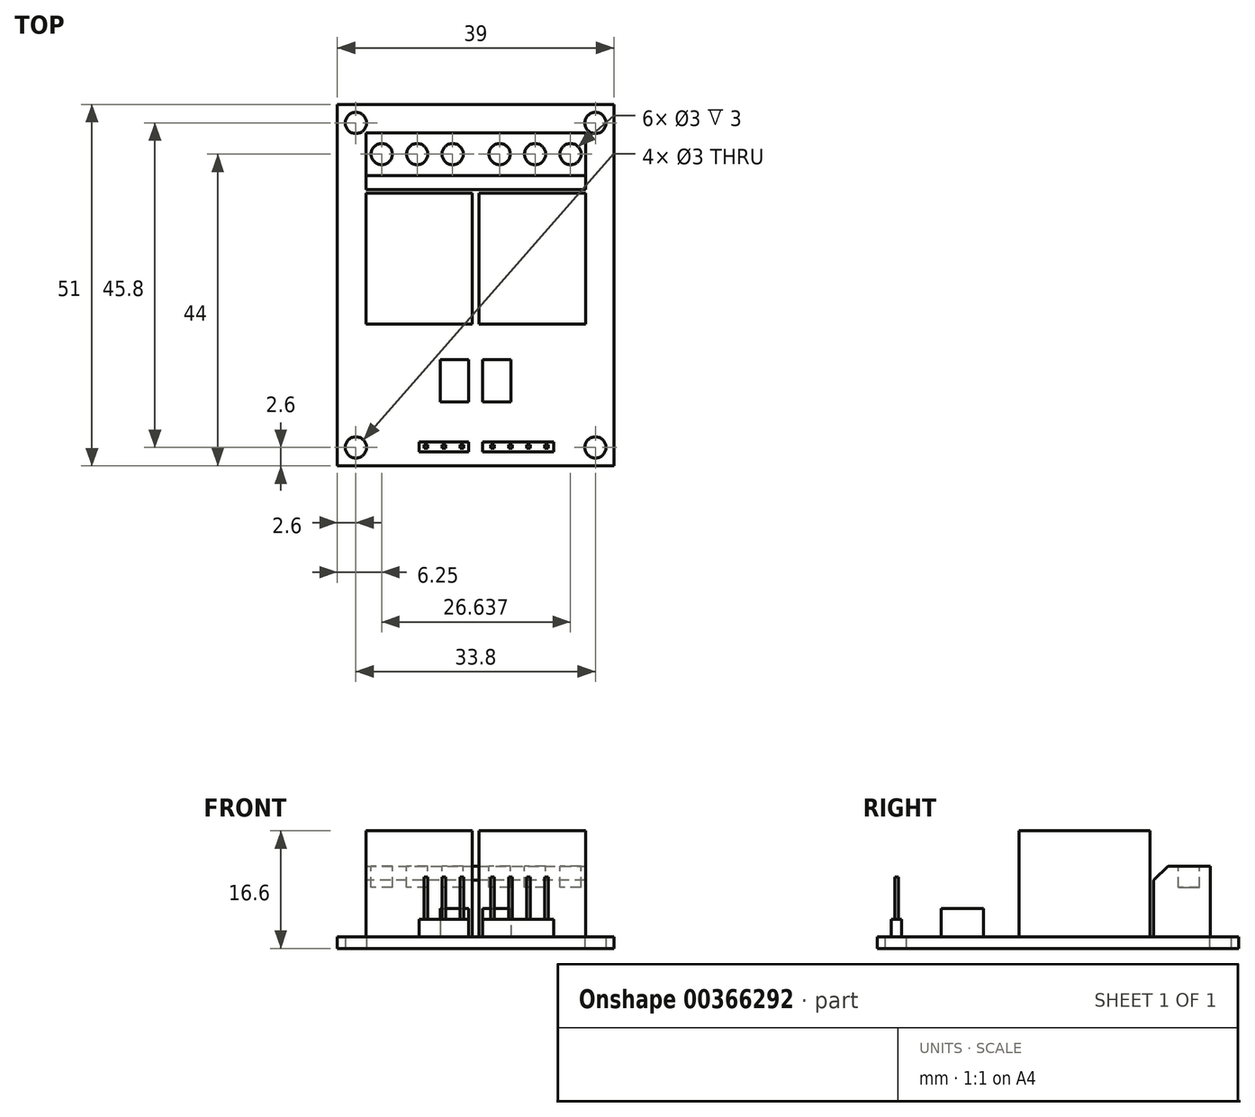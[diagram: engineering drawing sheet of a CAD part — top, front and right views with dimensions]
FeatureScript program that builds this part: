
annotation { "Feature Type Name" : "Feature", "Feature Type Description" : "" }
export const myFeature = defineFeature(function(context is Context, id is Id, definition is map)
    precondition{}
    {
        {
            var Q0;
            Q0=qCreatedBy(makeId("Top.planeOp"),FACE);
            var sketch = newSketch(context, id + "F0", { "sketchPlane" : qUnion([Q0])});
            skLineSegment(sketch, "E0.bottom", {"start": v(19.5, -25.5) * mm, "end": v(-19.5, -25.5) * mm});
            skLineSegment(sketch, "E0.top", {"start": v(19.5, 25.5) * mm, "end": v(-19.5, 25.5) * mm});
            skLineSegment(sketch, "E0.left", {"start": v(19.5, -25.5) * mm, "end": v(19.5, 25.5) * mm});
            skLineSegment(sketch, "E0.right", {"start": v(-19.5, -25.5) * mm, "end": v(-19.5, 25.5) * mm});
            skPoint(sketch, "E0.middle", {"position": v(0, 0) * mm});
            skPoint(sketch, "E1", {"position": v(-16.9, 22.9) * mm});
            skPoint(sketch, "E2", {"position": v(16.9, 22.9) * mm});
            skPoint(sketch, "E3", {"position": v(16.9, -22.9) * mm});
            skPoint(sketch, "E4", {"position": v(-16.9, -22.9) * mm});
            skCircle(sketch, "E5", {"center": v(-16.9, 22.9) * mm, "radius": 1.5 * mm});
            skCircle(sketch, "E6", {"center": v(16.9, 22.9) * mm, "radius": 1.5 * mm});
            skCircle(sketch, "E7", {"center": v(16.9, -22.9) * mm, "radius": 1.5 * mm});
            skCircle(sketch, "E8", {"center": v(-16.9, -22.9) * mm, "radius": 1.5 * mm});
            skSolve(sketch);
        }
        {
            var Q0;
            Q0=makeQuery(id+"F0.imprint","IMPRINT",FACE,{"disambiguationData":[TD([[makeQuery(id+"F0.imprint","IMPRINT",EDGE,{"derivedFrom":sQuery(id+"F0.wireOp",EDGE,"E0.bottom")}),-1.0]])]});
            extrude(context, id + "F1", {"entities" : qUnion([Q0]), "depth" : 1.6 * mm});
        }
        {
            var Q0;
            Q0=makeQuery(id+"F1.opExtrude","CAP_FACE",FACE,{"disambiguationData":[OSD([sQuery(id+"F0.wireOp",EDGE,"E0.bottom"),sQuery(id+"F0.wireOp",EDGE,"E0.top"),sQuery(id+"F0.wireOp",EDGE,"E0.left"),sQuery(id+"F0.wireOp",EDGE,"E0.right"),sQuery(id+"F0.wireOp",EDGE,"E5"),sQuery(id+"F0.wireOp",EDGE,"E6"),sQuery(id+"F0.wireOp",EDGE,"E7"),sQuery(id+"F0.wireOp",EDGE,"E8")])],"isStart":false});
            var sketch = newSketch(context, id + "F2", { "sketchPlane" : qUnion([Q0])});
            skLineSegment(sketch, "E9.bottom", {"start": v(-15.5, 13) * mm, "end": v(-0.5, 13) * mm});
            skLineSegment(sketch, "E9.top", {"start": v(-15.5, -5.5) * mm, "end": v(-0.5, -5.5) * mm});
            skLineSegment(sketch, "E9.left", {"start": v(-15.5, 13) * mm, "end": v(-15.5, -5.5) * mm});
            skLineSegment(sketch, "E9.right", {"start": v(-0.5, 13) * mm, "end": v(-0.5, -5.5) * mm});
            skLineSegment(sketch, "E10.bottom", {"start": v(0.5, 13) * mm, "end": v(15.5, 13) * mm});
            skLineSegment(sketch, "E10.top", {"start": v(0.5, -5.5) * mm, "end": v(15.5, -5.5) * mm});
            skLineSegment(sketch, "E10.left", {"start": v(0.5, 13) * mm, "end": v(0.5, -5.5) * mm});
            skLineSegment(sketch, "E10.right", {"start": v(15.5, 13) * mm, "end": v(15.5, -5.5) * mm});
            skSolve(sketch);
        }
        {
            var Q0;
            Q0=makeQuery(id+"F2.imprint","IMPRINT",FACE,{"disambiguationData":[TD([[makeQuery(id+"F2.imprint","IMPRINT",EDGE,{"derivedFrom":sQuery(id+"F2.wireOp",EDGE,"E9.bottom")}),-1.0]])]});
            var Q1;
            Q1=makeQuery(id+"F2.imprint","IMPRINT",FACE,{"disambiguationData":[TD([[makeQuery(id+"F2.imprint","IMPRINT",EDGE,{"derivedFrom":sQuery(id+"F2.wireOp",EDGE,"E10.bottom")}),-1.0]])]});
            extrude(context, id + "F3", {"entities" : qUnion([Q0, Q1]), "operationType" : NewBodyOperationType.ADD, "depth" : 15 * mm});
        }
        {
            var Q0;
            Q0=makeQuery(id+"F1.opExtrude","CAP_FACE",FACE,{"disambiguationData":[OSD([sQuery(id+"F0.wireOp",EDGE,"E0.bottom"),sQuery(id+"F0.wireOp",EDGE,"E0.top"),sQuery(id+"F0.wireOp",EDGE,"E0.left"),sQuery(id+"F0.wireOp",EDGE,"E0.right"),sQuery(id+"F0.wireOp",EDGE,"E5"),sQuery(id+"F0.wireOp",EDGE,"E6"),sQuery(id+"F0.wireOp",EDGE,"E7"),sQuery(id+"F0.wireOp",EDGE,"E8")])],"isStart":false});
            var sketch = newSketch(context, id + "F4", { "sketchPlane" : qUnion([Q0])});
            skLineSegment(sketch, "E11.bottom", {"start": v(-15.5, 21.5) * mm, "end": v(15.5, 21.5) * mm});
            skLineSegment(sketch, "E11.top", {"start": v(-15.5, 13.5) * mm, "end": v(15.5, 13.5) * mm});
            skLineSegment(sketch, "E11.left", {"start": v(-15.5, 21.5) * mm, "end": v(-15.5, 13.5) * mm});
            skLineSegment(sketch, "E11.right", {"start": v(15.5, 21.5) * mm, "end": v(15.5, 13.5) * mm});
            skSolve(sketch);
        }
        {
            var Q0;
            Q0=makeQuery(id+"F4.imprint","IMPRINT",FACE,{"disambiguationData":[TD([[makeQuery(id+"F4.imprint","IMPRINT",EDGE,{"derivedFrom":sQuery(id+"F4.wireOp",EDGE,"E11.bottom")}),-1.0]])]});
            extrude(context, id + "F5", {"entities" : qUnion([Q0]), "operationType" : NewBodyOperationType.ADD, "depth" : 10 * mm});
        }
        {
            var Q0;
            Q0=makeQuery(id+"F5.opExtrude","CAP_EDGE",EDGE,{"disambiguationData":[OSD([sQuery(id+"F4.wireOp",EDGE,"E11.top")])],"isStart":false});
            chamfer(context, id + "F6", {"entities" : qUnion([Q0]), "width" : 2 * mm, "tangentPropagation" : true});
        }
        {
            var Q0;
            Q0=makeQuery(id+"F5.opExtrude","CAP_FACE",FACE,{"disambiguationData":[OSD([sQuery(id+"F4.wireOp",EDGE,"E11.bottom"),sQuery(id+"F4.wireOp",EDGE,"E11.top"),sQuery(id+"F4.wireOp",EDGE,"E11.left"),sQuery(id+"F4.wireOp",EDGE,"E11.right")])],"isStart":false});
            var sketch = newSketch(context, id + "F7", { "sketchPlane" : qUnion([Q0])});
            skCircle(sketch, "E12", {"center": v(-13.25, 18.5) * mm, "radius": 1.5 * mm});
            skCircle(sketch, "E13", {"center": v(-8.25, 18.5) * mm, "radius": 1.5 * mm});
            skCircle(sketch, "E14", {"center": v(-3.25, 18.5) * mm, "radius": 1.5 * mm});
            skCircle(sketch, "E15", {"center": v(3.39, 18.5) * mm, "radius": 1.5 * mm});
            skCircle(sketch, "E16", {"center": v(8.39, 18.5) * mm, "radius": 1.5 * mm});
            skCircle(sketch, "E17", {"center": v(13.39, 18.5) * mm, "radius": 1.5 * mm});
            skSolve(sketch);
        }
        {
            var Q0;
            Q0=makeQuery(id+"F7.imprint","IMPRINT",FACE,{"disambiguationData":[TD([[makeQuery(id+"F7.imprint","IMPRINT",EDGE,{"derivedFrom":sQuery(id+"F7.wireOp",EDGE,"E12")}),1.0]])]});
            var Q1;
            Q1=makeQuery(id+"F7.imprint","IMPRINT",FACE,{"disambiguationData":[TD([[makeQuery(id+"F7.imprint","IMPRINT",EDGE,{"derivedFrom":sQuery(id+"F7.wireOp",EDGE,"E13")}),1.0]])]});
            var Q2;
            Q2=makeQuery(id+"F7.imprint","IMPRINT",FACE,{"disambiguationData":[TD([[makeQuery(id+"F7.imprint","IMPRINT",EDGE,{"derivedFrom":sQuery(id+"F7.wireOp",EDGE,"E14")}),1.0]])]});
            var Q3;
            Q3=makeQuery(id+"F7.imprint","IMPRINT",FACE,{"disambiguationData":[TD([[makeQuery(id+"F7.imprint","IMPRINT",EDGE,{"derivedFrom":sQuery(id+"F7.wireOp",EDGE,"E15")}),1.0]])]});
            var Q4;
            Q4=makeQuery(id+"F7.imprint","IMPRINT",FACE,{"disambiguationData":[TD([[makeQuery(id+"F7.imprint","IMPRINT",EDGE,{"derivedFrom":sQuery(id+"F7.wireOp",EDGE,"E16")}),1.0]])]});
            var Q5;
            Q5=makeQuery(id+"F7.imprint","IMPRINT",FACE,{"disambiguationData":[TD([[makeQuery(id+"F7.imprint","IMPRINT",EDGE,{"derivedFrom":sQuery(id+"F7.wireOp",EDGE,"E17")}),1.0]])]});
            extrude(context, id + "F8", {"entities" : qUnion([Q0, Q1, Q2, Q3, Q4, Q5]), "operationType" : NewBodyOperationType.REMOVE, "oppositeDirection" : true, "depth" : 3 * mm});
        }
        {
            var Q0;
            Q0=makeQuery(id+"F1.opExtrude","CAP_FACE",FACE,{"disambiguationData":[OSD([sQuery(id+"F0.wireOp",EDGE,"E0.bottom"),sQuery(id+"F0.wireOp",EDGE,"E0.top"),sQuery(id+"F0.wireOp",EDGE,"E0.left"),sQuery(id+"F0.wireOp",EDGE,"E0.right"),sQuery(id+"F0.wireOp",EDGE,"E5"),sQuery(id+"F0.wireOp",EDGE,"E6"),sQuery(id+"F0.wireOp",EDGE,"E7"),sQuery(id+"F0.wireOp",EDGE,"E8")])],"isStart":false});
            var sketch = newSketch(context, id + "F9", { "sketchPlane" : qUnion([Q0])});
            skLineSegment(sketch, "E18.bottom", {"start": v(-5, -10.5) * mm, "end": v(-1, -10.5) * mm});
            skLineSegment(sketch, "E18.top", {"start": v(-5, -16.5) * mm, "end": v(-1, -16.5) * mm});
            skLineSegment(sketch, "E18.left", {"start": v(-5, -10.5) * mm, "end": v(-5, -16.5) * mm});
            skLineSegment(sketch, "E18.right", {"start": v(-1, -10.5) * mm, "end": v(-1, -16.5) * mm});
            skLineSegment(sketch, "E19.bottom", {"start": v(1, -10.5) * mm, "end": v(5, -10.5) * mm});
            skLineSegment(sketch, "E19.top", {"start": v(1, -16.5) * mm, "end": v(5, -16.5) * mm});
            skLineSegment(sketch, "E19.left", {"start": v(1, -10.5) * mm, "end": v(1, -16.5) * mm});
            skLineSegment(sketch, "E19.right", {"start": v(5, -10.5) * mm, "end": v(5, -16.5) * mm});
            skSolve(sketch);
        }
        {
            var Q0;
            Q0=makeQuery(id+"F9.imprint","IMPRINT",FACE,{"disambiguationData":[TD([[makeQuery(id+"F9.imprint","IMPRINT",EDGE,{"derivedFrom":sQuery(id+"F9.wireOp",EDGE,"E18.bottom")}),-1.0]])]});
            var Q1;
            Q1=makeQuery(id+"F9.imprint","IMPRINT",FACE,{"disambiguationData":[TD([[makeQuery(id+"F9.imprint","IMPRINT",EDGE,{"derivedFrom":sQuery(id+"F9.wireOp",EDGE,"E19.bottom")}),-1.0]])]});
            extrude(context, id + "F10", {"entities" : qUnion([Q0, Q1]), "operationType" : NewBodyOperationType.ADD, "depth" : 4 * mm});
        }
        {
            var Q0;
            Q0=makeQuery(id+"F1.opExtrude","CAP_FACE",FACE,{"disambiguationData":[OSD([sQuery(id+"F0.wireOp",EDGE,"E0.bottom"),sQuery(id+"F0.wireOp",EDGE,"E0.top"),sQuery(id+"F0.wireOp",EDGE,"E0.left"),sQuery(id+"F0.wireOp",EDGE,"E0.right"),sQuery(id+"F0.wireOp",EDGE,"E5"),sQuery(id+"F0.wireOp",EDGE,"E6"),sQuery(id+"F0.wireOp",EDGE,"E7"),sQuery(id+"F0.wireOp",EDGE,"E8")])],"isStart":false});
            var sketch = newSketch(context, id + "F11", { "sketchPlane" : qUnion([Q0])});
            skLineSegment(sketch, "E20.bottom", {"start": v(1, -23.5) * mm, "end": v(11, -23.5) * mm});
            skLineSegment(sketch, "E20.top", {"start": v(1, -22.1) * mm, "end": v(11, -22.1) * mm});
            skLineSegment(sketch, "E20.left", {"start": v(1, -23.5) * mm, "end": v(1, -22.1) * mm});
            skLineSegment(sketch, "E20.right", {"start": v(11, -23.5) * mm, "end": v(11, -22.1) * mm});
            skLineSegment(sketch, "E21.bottom", {"start": v(-1, -23.5) * mm, "end": v(-8, -23.5) * mm});
            skLineSegment(sketch, "E21.top", {"start": v(-1, -22.1) * mm, "end": v(-8, -22.1) * mm});
            skLineSegment(sketch, "E21.left", {"start": v(-1, -23.5) * mm, "end": v(-1, -22.1) * mm});
            skLineSegment(sketch, "E21.right", {"start": v(-8, -23.5) * mm, "end": v(-8, -22.1) * mm});
            skSolve(sketch);
        }
        {
            var Q0;
            Q0=makeQuery(id+"F11.imprint","IMPRINT",FACE,{"disambiguationData":[TD([[makeQuery(id+"F11.imprint","IMPRINT",EDGE,{"derivedFrom":sQuery(id+"F11.wireOp",EDGE,"E21.bottom")}),-1.0]])]});
            var Q1;
            Q1=makeQuery(id+"F11.imprint","IMPRINT",FACE,{"disambiguationData":[TD([[makeQuery(id+"F11.imprint","IMPRINT",EDGE,{"derivedFrom":sQuery(id+"F11.wireOp",EDGE,"E20.bottom")}),1.0]])]});
            extrude(context, id + "F12", {"entities" : qUnion([Q0, Q1]), "operationType" : NewBodyOperationType.ADD, "depth" : 2.5 * mm});
        }
        {
            var Q0;
            Q0=makeQuery(id+"F12.opExtrude","CAP_FACE",FACE,{"disambiguationData":[OSD([sQuery(id+"F11.wireOp",EDGE,"E20.bottom"),sQuery(id+"F11.wireOp",EDGE,"E20.top"),sQuery(id+"F11.wireOp",EDGE,"E20.left"),sQuery(id+"F11.wireOp",EDGE,"E20.right")])],"isStart":false});
            var sketch = newSketch(context, id + "F13", { "sketchPlane" : qUnion([Q0])});
            skLineSegment(sketch, "E22.bottom", {"start": v(-7.25, -22.5) * mm, "end": v(-6.75, -22.5) * mm});
            skLineSegment(sketch, "E22.top", {"start": v(-7.25, -23) * mm, "end": v(-6.75, -23) * mm});
            skLineSegment(sketch, "E22.left", {"start": v(-7.25, -22.5) * mm, "end": v(-7.25, -23) * mm});
            skLineSegment(sketch, "E22.right", {"start": v(-6.75, -22.5) * mm, "end": v(-6.75, -23) * mm});
            skLineSegment(sketch, "E23.bottom", {"start": v(-2.17, -22.5) * mm, "end": v(-1.67, -22.5) * mm});
            skLineSegment(sketch, "E23.top", {"start": v(-2.17, -23) * mm, "end": v(-1.67, -23) * mm});
            skLineSegment(sketch, "E23.left", {"start": v(-2.17, -22.5) * mm, "end": v(-2.17, -23) * mm});
            skLineSegment(sketch, "E23.right", {"start": v(-1.67, -22.5) * mm, "end": v(-1.67, -23) * mm});
            skLineSegment(sketch, "E24.bottom", {"start": v(-4.7, -22.5) * mm, "end": v(-4.2, -22.5) * mm});
            skLineSegment(sketch, "E24.top", {"start": v(-4.7, -23) * mm, "end": v(-4.2, -23) * mm});
            skLineSegment(sketch, "E24.left", {"start": v(-4.7, -22.5) * mm, "end": v(-4.7, -23) * mm});
            skLineSegment(sketch, "E24.right", {"start": v(-4.2, -22.5) * mm, "end": v(-4.2, -23) * mm});
            skLineSegment(sketch, "E25.bottom", {"start": v(2.13, -22.5) * mm, "end": v(2.63, -22.5) * mm});
            skLineSegment(sketch, "E25.top", {"start": v(2.13, -23) * mm, "end": v(2.63, -23) * mm});
            skLineSegment(sketch, "E25.left", {"start": v(2.13, -22.5) * mm, "end": v(2.13, -23) * mm});
            skLineSegment(sketch, "E25.right", {"start": v(2.63, -22.5) * mm, "end": v(2.63, -23) * mm});
            skLineSegment(sketch, "E26.bottom", {"start": v(4.67, -22.5) * mm, "end": v(5.17, -22.5) * mm});
            skLineSegment(sketch, "E26.top", {"start": v(4.67, -23) * mm, "end": v(5.17, -23) * mm});
            skLineSegment(sketch, "E26.left", {"start": v(4.67, -22.5) * mm, "end": v(4.67, -23) * mm});
            skLineSegment(sketch, "E26.right", {"start": v(5.17, -22.5) * mm, "end": v(5.17, -23) * mm});
            skLineSegment(sketch, "E27.bottom", {"start": v(7.2, -22.5) * mm, "end": v(7.71, -22.5) * mm});
            skLineSegment(sketch, "E27.top", {"start": v(7.2, -23) * mm, "end": v(7.71, -23) * mm});
            skLineSegment(sketch, "E27.left", {"start": v(7.2, -22.5) * mm, "end": v(7.2, -23) * mm});
            skLineSegment(sketch, "E27.right", {"start": v(7.71, -22.5) * mm, "end": v(7.71, -23) * mm});
            skLineSegment(sketch, "E28.bottom", {"start": v(9.75, -22.5) * mm, "end": v(10.25, -22.5) * mm});
            skLineSegment(sketch, "E28.top", {"start": v(9.75, -23) * mm, "end": v(10.25, -23) * mm});
            skLineSegment(sketch, "E28.left", {"start": v(9.75, -22.5) * mm, "end": v(9.75, -23) * mm});
            skLineSegment(sketch, "E28.right", {"start": v(10.25, -22.5) * mm, "end": v(10.25, -23) * mm});
            skSolve(sketch);
        }
        {
            var Q0;
            Q0=makeQuery(id+"F13.imprint","IMPRINT",FACE,{"disambiguationData":[TD([[makeQuery(id+"F13.imprint","IMPRINT",EDGE,{"derivedFrom":sQuery(id+"F13.wireOp",EDGE,"E22.bottom")}),-1.0]])]});
            var Q1;
            Q1=makeQuery(id+"F13.imprint","IMPRINT",FACE,{"disambiguationData":[TD([[makeQuery(id+"F13.imprint","IMPRINT",EDGE,{"derivedFrom":sQuery(id+"F13.wireOp",EDGE,"E24.bottom")}),-1.0]])]});
            var Q2;
            Q2=makeQuery(id+"F13.imprint","IMPRINT",FACE,{"disambiguationData":[TD([[makeQuery(id+"F13.imprint","IMPRINT",EDGE,{"derivedFrom":sQuery(id+"F13.wireOp",EDGE,"E23.bottom")}),-1.0]])]});
            var Q3;
            Q3=makeQuery(id+"F13.imprint","IMPRINT",FACE,{"disambiguationData":[TD([[makeQuery(id+"F13.imprint","IMPRINT",EDGE,{"derivedFrom":sQuery(id+"F13.wireOp",EDGE,"E25.bottom")}),-1.0]])]});
            var Q4;
            Q4=makeQuery(id+"F13.imprint","IMPRINT",FACE,{"disambiguationData":[TD([[makeQuery(id+"F13.imprint","IMPRINT",EDGE,{"derivedFrom":sQuery(id+"F13.wireOp",EDGE,"E26.bottom")}),-1.0]])]});
            var Q5;
            Q5=makeQuery(id+"F13.imprint","IMPRINT",FACE,{"disambiguationData":[TD([[makeQuery(id+"F13.imprint","IMPRINT",EDGE,{"derivedFrom":sQuery(id+"F13.wireOp",EDGE,"E27.bottom")}),-1.0]])]});
            var Q6;
            Q6=makeQuery(id+"F13.imprint","IMPRINT",FACE,{"disambiguationData":[TD([[makeQuery(id+"F13.imprint","IMPRINT",EDGE,{"derivedFrom":sQuery(id+"F13.wireOp",EDGE,"E28.bottom")}),-1.0]])]});
            extrude(context, id + "F14", {"entities" : qUnion([Q0, Q1, Q2, Q3, Q4, Q5, Q6]), "operationType" : NewBodyOperationType.ADD, "depth" : 6 * mm});
        }
    });
